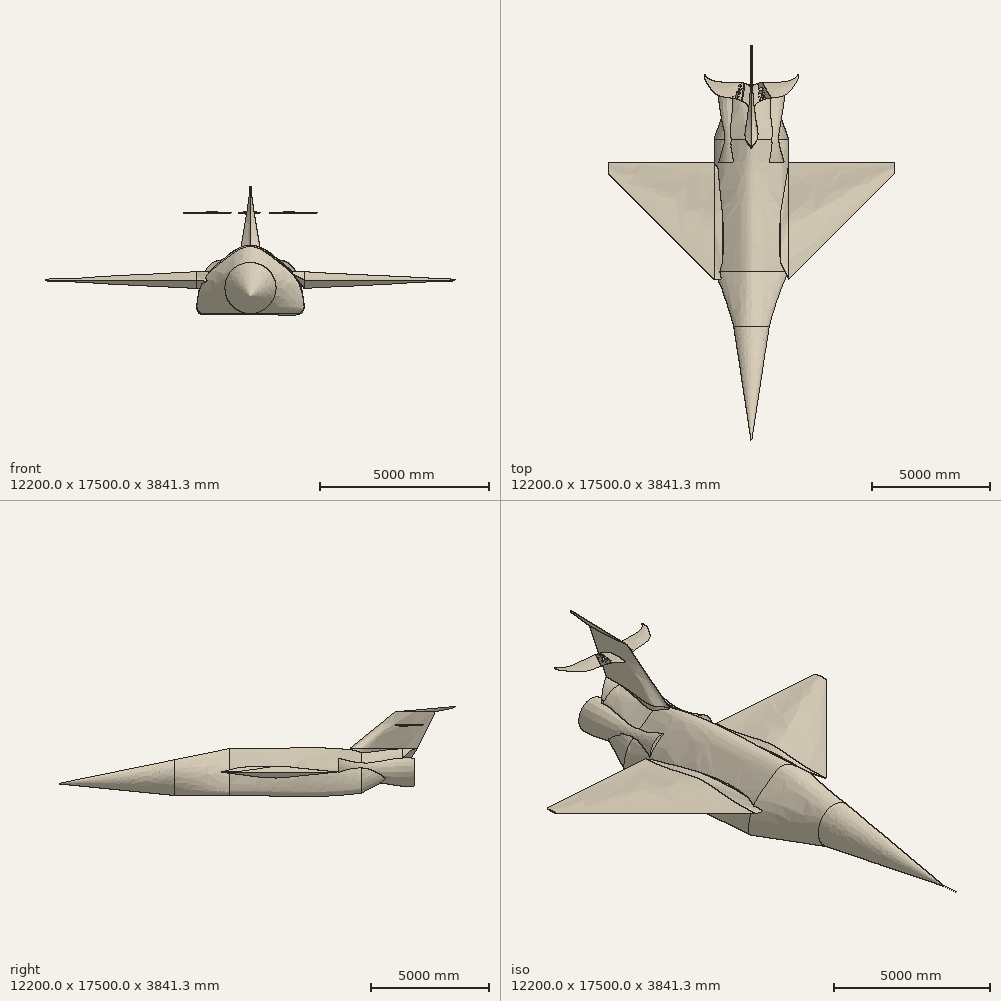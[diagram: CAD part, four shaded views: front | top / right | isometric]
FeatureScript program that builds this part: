
annotation { "Feature Type Name" : "Feature", "Feature Type Description" : "" }
export const myFeature = defineFeature(function(context is Context, id is Id, definition is map)
    precondition{}
    {
        {
            var Q0;
            Q0=qCreatedBy(makeId("Right.planeOp"),FACE);
            var sketch = newSketch(context, id + "F0", { "sketchPlane" : qUnion([Q0])});
            skLineSegment(sketch, "E0", {"start": v(0, 0) * mm, "end": v(-1750, 0) * mm});
            skLineSegment(sketch, "E1", {"start": v(-1750, 0) * mm, "end": v(-3500, 0) * mm});
            skLineSegment(sketch, "E2", {"start": v(-3500, 0) * mm, "end": v(-3500, -1000) * mm});
            skLineSegment(sketch, "E3", {"start": v(-3500, -1000) * mm, "end": v(-8500, -1000) * mm});
            skLineSegment(sketch, "E4", {"start": v(-8500, -1000) * mm, "end": v(-8500, -499.31) * mm});
            skLineSegment(sketch, "E5", {"start": v(-1151.4, 0) * mm, "end": v(-1151.4, 1000) * mm});
            skLineSegment(sketch, "E6", {"start": v(-1151.4, 1000) * mm, "end": v(-8500, -499.31) * mm});
            skLineSegment(sketch, "E7", {"start": v(-8500, -499.31) * mm, "end": v(-3500, -1000) * mm});
            skLineSegment(sketch, "E8", {"start": v(-3500, 0) * mm, "end": v(-3500, 520.82) * mm});
            skLineSegment(sketch, "E9", {"start": v(-8500, -499.31) * mm, "end": v(-8450, -499.31) * mm});
            skLineSegment(sketch, "E10", {"start": v(-8450, -499.31) * mm, "end": v(-8450, -489.1) * mm});
            skLineSegment(sketch, "E11", {"start": v(-8450, -499.31) * mm, "end": v(-8450, -504.32) * mm});
            skSolve(sketch);
        }
        {
            var Q0;
            Q0=sQuery(id+"F0.wireOp",EDGE,"E5");
            cPlane(context, id + "F1", {"entities" : qUnion([Q0]), "cplaneType" : CPlaneType.LINE_ANGLE, "offset" : 25 * mm, "angle" : 90 * degree, "oppositeDirection" : true, "width" : 150 * mm, "height" : 150 * mm});
        }
        {
            var Q0;
            Q0=qCreatedBy(id+"F1.planeOp",FACE);
            var sketch = newSketch(context, id + "F2", { "sketchPlane" : qUnion([Q0])});
            skLineSegment(sketch, "E12.top", {"start": v(-1394.2, -1000) * mm, "end": v(1394.2, -1000) * mm});
            skPoint(sketch, "E12.middle", {"position": v(0, 0) * mm});
            skFitSpline(sketch, "E13", {"points": [v(-1600, -1000) * mm, v(-848, 530) * mm, v(0, 1000) * mm, v(848, 530) * mm, v(1600, -1000) * mm], "startDerivative": vector(0, 10524.75) * mm, "endDerivative": vector(0, -10524.75) * mm});
            skArc(sketch, "E14", {"start": v(-735.27, 618.52) * mm, "mid": v(-1273.27, 435.52) * mm, "end": v(-1440.68, -107.53) * mm});
            skArc(sketch, "E15", {"start": v(1440.68, -107.53) * mm, "mid": v(1273.27, 435.52) * mm, "end": v(735.27, 618.52) * mm});
            skFitSpline(sketch, "E16.trimOffspring", {"points": [v(-1600, -1000) * mm, v(-848, 530) * mm, v(0, 1000) * mm, v(848, 530) * mm, v(1600, -1000) * mm], "startDerivative": vector(0, 10524.75) * mm, "endDerivative": vector(0, -10524.75) * mm});
            skFitSpline(sketch, "E17.trimOffspring", {"points": [v(-1600, -1000) * mm, v(-848, 530) * mm, v(0, 1000) * mm, v(848, 530) * mm, v(1600, -1000) * mm], "startDerivative": vector(0, 10524.75) * mm, "endDerivative": vector(0, -10524.75) * mm});
            skArc(sketch, "E18.filletArc", {"start": v(-1593.82, -787.83) * mm, "mid": v(-1539.85, -937.05) * mm, "end": v(-1394.2, -1000) * mm});
            skArc(sketch, "E19.filletArc", {"start": v(1394.2, -1000) * mm, "mid": v(1539.85, -937.05) * mm, "end": v(1593.82, -787.83) * mm});
            skSolve(sketch);
        }
        {
            var Q0;
            Q0=qCreatedBy(makeId("Front.planeOp"),FACE);
            var sketch = newSketch(context, id + "F3", { "sketchPlane" : qUnion([Q0])});
            skLineSegment(sketch, "E20.top", {"start": v(-1394.2, -1000) * mm, "end": v(1394.2, -1000) * mm});
            skPoint(sketch, "E20.middle", {"position": v(0, 0) * mm});
            skFitSpline(sketch, "E21", {"points": [v(-1600, -1000) * mm, v(-848, 530) * mm, v(0, 1000) * mm, v(848, 530) * mm, v(1600, -1000) * mm], "startDerivative": vector(0, 10524.75) * mm, "endDerivative": vector(0, -10524.75) * mm});
            skArc(sketch, "E22", {"start": v(-735.27, 618.52) * mm, "mid": v(-1273.27, 435.52) * mm, "end": v(-1440.68, -107.53) * mm});
            skArc(sketch, "E23", {"start": v(1440.68, -107.53) * mm, "mid": v(1273.27, 435.52) * mm, "end": v(735.27, 618.52) * mm});
            skFitSpline(sketch, "E24.trimOffspring", {"points": [v(-1600, -1000) * mm, v(-848, 530) * mm, v(0, 1000) * mm, v(848, 530) * mm, v(1600, -1000) * mm], "startDerivative": vector(0, 10524.75) * mm, "endDerivative": vector(0, -10524.75) * mm});
            skFitSpline(sketch, "E25.trimOffspring", {"points": [v(-1600, -1000) * mm, v(-848, 530) * mm, v(0, 1000) * mm, v(848, 530) * mm, v(1600, -1000) * mm], "startDerivative": vector(0, 10524.75) * mm, "endDerivative": vector(0, -10524.75) * mm});
            skArc(sketch, "E26.filletArc", {"start": v(-1593.82, -787.83) * mm, "mid": v(-1539.85, -937.05) * mm, "end": v(-1394.2, -1000) * mm});
            skArc(sketch, "E27.filletArc", {"start": v(1394.2, -1000) * mm, "mid": v(1539.85, -937.05) * mm, "end": v(1593.82, -787.83) * mm});
            skSolve(sketch);
        }
        {
            var Q0;
            Q0=qCreatedBy(makeId("Front.planeOp"),FACE);
            cPlane(context, id + "F4", {"entities" : qUnion([Q0]), "cplaneType" : CPlaneType.OFFSET, "offset" : 3500 * mm, "oppositeDirection" : true, "width" : 150 * mm, "height" : 150 * mm});
        }
        {
            var Q0;
            Q0=qCreatedBy(id+"F4.planeOp",FACE);
            var sketch = newSketch(context, id + "F5", { "sketchPlane" : qUnion([Q0])});
            skLineSegment(sketch, "E28.top", {"start": v(-1394.2, -1000) * mm, "end": v(1394.2, -1000) * mm});
            skPoint(sketch, "E28.middle", {"position": v(0, 0) * mm});
            skFitSpline(sketch, "E29", {"points": [v(-1600, -1000) * mm, v(-848, 530) * mm, v(0, 1000) * mm, v(848, 530) * mm, v(1600, -1000) * mm], "startDerivative": vector(0, 10524.75) * mm, "endDerivative": vector(0, -10524.75) * mm});
            skArc(sketch, "E30", {"start": v(-735.27, 618.52) * mm, "mid": v(-1273.27, 435.52) * mm, "end": v(-1440.68, -107.53) * mm});
            skArc(sketch, "E31", {"start": v(1440.68, -107.53) * mm, "mid": v(1273.27, 435.52) * mm, "end": v(735.27, 618.52) * mm});
            skFitSpline(sketch, "E32.trimOffspring", {"points": [v(-1600, -1000) * mm, v(-848, 530) * mm, v(0, 1000) * mm, v(848, 530) * mm, v(1600, -1000) * mm], "startDerivative": vector(0, 10524.75) * mm, "endDerivative": vector(0, -10524.75) * mm});
            skFitSpline(sketch, "E33.trimOffspring", {"points": [v(-1600, -1000) * mm, v(-848, 530) * mm, v(0, 1000) * mm, v(848, 530) * mm, v(1600, -1000) * mm], "startDerivative": vector(0, 10524.75) * mm, "endDerivative": vector(0, -10524.75) * mm});
            skArc(sketch, "E34.filletArc", {"start": v(-1593.82, -787.83) * mm, "mid": v(-1539.85, -937.05) * mm, "end": v(-1394.2, -1000) * mm});
            skArc(sketch, "E35.filletArc", {"start": v(1394.2, -1000) * mm, "mid": v(1539.85, -937.05) * mm, "end": v(1593.82, -787.83) * mm});
            skSolve(sketch);
        }
        {
            var Q0;
            Q0=qCreatedBy(makeId("Front.planeOp"),FACE);
            cPlane(context, id + "F6", {"entities" : qUnion([Q0]), "cplaneType" : CPlaneType.OFFSET, "offset" : 4500 * mm, "oppositeDirection" : true, "width" : 150 * mm, "height" : 150 * mm});
        }
        {
            var Q0;
            Q0=qCreatedBy(id+"F6.planeOp",FACE);
            var sketch = newSketch(context, id + "F7", { "sketchPlane" : qUnion([Q0])});
            skLineSegment(sketch, "E36.top", {"start": v(-1413.07, -900) * mm, "end": v(1413.07, -900) * mm});
            skPoint(sketch, "E36.middle", {"position": v(0, 0) * mm});
            skFitSpline(sketch, "E37", {"points": [v(-1600, -900) * mm, v(-784.42, 441.24) * mm, v(0, 900) * mm, v(784.42, 441.24) * mm, v(1600, -900) * mm], "startDerivative": vector(0, 9508.62) * mm, "endDerivative": vector(0, -9508.62) * mm});
            skArc(sketch, "E38", {"start": v(-719.25, 488.69) * mm, "mid": v(-1131.76, 394.84) * mm, "end": v(-1324.66, 18.33) * mm});
            skArc(sketch, "E39", {"start": v(1324.66, 18.33) * mm, "mid": v(1131.76, 394.84) * mm, "end": v(719.25, 488.69) * mm});
            skFitSpline(sketch, "E40.trimOffspring", {"points": [v(-1600, -900) * mm, v(-784.42, 441.24) * mm, v(0, 900) * mm, v(784.42, 441.24) * mm, v(1600, -900) * mm], "startDerivative": vector(0, 9508.62) * mm, "endDerivative": vector(0, -9508.62) * mm});
            skFitSpline(sketch, "E41.trimOffspring", {"points": [v(-1600, -900) * mm, v(-784.42, 441.24) * mm, v(0, 900) * mm, v(784.42, 441.24) * mm, v(1600, -900) * mm], "startDerivative": vector(0, 9508.62) * mm, "endDerivative": vector(0, -9508.62) * mm});
            skArc(sketch, "E42.filletArc", {"start": v(-1592.48, -705.43) * mm, "mid": v(-1545.4, -842.02) * mm, "end": v(-1413.07, -900) * mm});
            skArc(sketch, "E43.filletArc", {"start": v(1413.07, -900) * mm, "mid": v(1545.4, -842.02) * mm, "end": v(1592.48, -705.43) * mm});
            skLineSegment(sketch, "E44", {"start": v(-719.25, 488.69) * mm, "end": v(-1324.66, 18.33) * mm, "construction": true});
            skLineSegment(sketch, "E45", {"start": v(719.25, 488.69) * mm, "end": v(1324.66, 18.33) * mm, "construction": true});
            skSolve(sketch);
        }
        {
            var Q0;
            Q0=qCreatedBy(makeId("Front.planeOp"),FACE);
            cPlane(context, id + "F8", {"entities" : qUnion([Q0]), "cplaneType" : CPlaneType.OFFSET, "offset" : 6232.05 * mm, "oppositeDirection" : true, "width" : 150 * mm, "height" : 150 * mm});
        }
        {
            var Q0;
            Q0=qCreatedBy(id+"F8.planeOp",FACE);
            var sketch = newSketch(context, id + "F9", { "sketchPlane" : qUnion([Q0])});
            skArc(sketch, "E46", {"start": v(998.61, 52.63) * mm, "mid": v(0, 1000) * mm, "end": v(-998.61, 52.63) * mm});
            skLineSegment(sketch, "E47", {"start": v(0, 0) * mm, "end": v(-948.68, 0) * mm});
            skLineSegment(sketch, "E48", {"start": v(0, 0) * mm, "end": v(948.68, 0) * mm});
            skLineSegment(sketch, "E49", {"start": v(0, 1000) * mm, "end": v(0, 675) * mm, "construction": true});
            skLineSegment(sketch, "E50", {"start": v(0, 675) * mm, "end": v(-737.82, 675) * mm, "construction": true});
            skLineSegment(sketch, "E51", {"start": v(0, 675) * mm, "end": v(737.82, 675) * mm, "construction": true});
            skPoint(sketch, "E52.visualSharp", {"position": v(-1000, 0) * mm});
            skArc(sketch, "E52.filletArc", {"start": v(-998.61, 52.63) * mm, "mid": v(-984.96, 15.59) * mm, "end": v(-948.68, 0) * mm});
            skPoint(sketch, "E53.visualSharp", {"position": v(1000, 0) * mm});
            skArc(sketch, "E53.filletArc", {"start": v(948.68, 0) * mm, "mid": v(984.96, 15.59) * mm, "end": v(998.61, 52.63) * mm});
            skSolve(sketch);
        }
        {
            var Q0;
            Q0=makeQuery(id+"F2.imprint","IMPRINT",FACE,{"disambiguationData":[TD([[makeQuery(id+"F2.imprint","IMPRINT",EDGE,{"derivedFrom":sQuery(id+"F2.wireOp",EDGE,"E12.top")}),1.0]])]});
            var Q1;
            Q1=makeQuery(id+"F3.imprint","IMPRINT",FACE,{"disambiguationData":[TD([[makeQuery(id+"F3.imprint","IMPRINT",EDGE,{"derivedFrom":sQuery(id+"F3.wireOp",EDGE,"E20.top")}),1.0]])]});
            var Q2;
            Q2=makeQuery(id+"F5.imprint","IMPRINT",FACE,{"disambiguationData":[TD([[makeQuery(id+"F5.imprint","IMPRINT",EDGE,{"derivedFrom":sQuery(id+"F5.wireOp",EDGE,"E28.top")}),1.0]])]});
            var Q3;
            Q3=makeQuery(id+"F7.imprint","IMPRINT",FACE,{"disambiguationData":[TD([[makeQuery(id+"F7.imprint","IMPRINT",EDGE,{"derivedFrom":sQuery(id+"F7.wireOp",EDGE,"E36.top")}),1.0]])]});
            loft(context, id + "F10", {"sheetProfilesArray" : [{ "sheetProfileEntities" : qUnion([Q0]) }, { "sheetProfileEntities" : qUnion([Q1]) }, { "sheetProfileEntities" : qUnion([Q2]) }, { "sheetProfileEntities" : qUnion([Q3]) }]});
        }
        {
            var Q0;
            Q0=sQuery(id+"F7.wireOp",EDGE,"E44");
            var Q1;
            Q1=sQuery(id+"F9.wireOp",VERTEX,"E50.end");
            cPlane(context, id + "F11", {"entities" : qUnion([Q0, Q1]), "cplaneType" : CPlaneType.LINE_ANGLE, "offset" : 25 * mm, "angle" : 180 * degree, "width" : 150 * mm, "height" : 150 * mm});
        }
        {
            var Q0;
            Q0=qCreatedBy(id+"F11.planeOp",FACE);
            var sketch = newSketch(context, id + "F12", { "sketchPlane" : qUnion([Q0])});
            skLineSegment(sketch, "E54", {"start": v(-589.34, 4526.34) * mm, "end": v(-612.8, 6268.32) * mm});
            skLineSegment(sketch, "E55", {"start": v(-1354.08, 4472.19) * mm, "end": v(-612.8, 6268.32) * mm});
            skSolve(sketch);
        }
        {
            var Q0;
            Q0=sQuery(id+"F7.wireOp",EDGE,"E45");
            var Q1;
            Q1=sQuery(id+"F9.wireOp",VERTEX,"E51.end");
            cPlane(context, id + "F13", {"entities" : qUnion([Q0, Q1]), "cplaneType" : CPlaneType.LINE_ANGLE, "offset" : 25 * mm, "angle" : 0 * degree, "width" : 150 * mm, "height" : 150 * mm});
        }
        {
            var Q0;
            Q0=qCreatedBy(id+"F13.planeOp",FACE);
            var sketch = newSketch(context, id + "F14", { "sketchPlane" : qUnion([Q0])});
            skLineSegment(sketch, "E56", {"start": v(589.34, 4526.34) * mm, "end": v(612.8, 6268.32) * mm});
            skLineSegment(sketch, "E57", {"start": v(1354.08, 4472.19) * mm, "end": v(612.8, 6268.32) * mm});
            skSolve(sketch);
        }
        {
            var Q1;
            Q1=makeQuery(id+"F10.opLoft","CAP_FACE",FACE,{"disambiguationData":[OSD([makeQuery(id+"F7.imprint","IMPRINT",FACE,{"disambiguationData":[TD([[makeQuery(id+"F7.imprint","IMPRINT",EDGE,{"derivedFrom":sQuery(id+"F7.wireOp",EDGE,"E36.top")}),1.0]])]})])],"isStart":true});
            var Q2;
            Q2=makeQuery(id+"F9.imprint","IMPRINT",FACE,{"disambiguationData":[TD([[makeQuery(id+"F9.imprint","IMPRINT",EDGE,{"derivedFrom":sQuery(id+"F9.wireOp",EDGE,"E46")}),1.0]])]});
            var Q3;
            Q3=sQuery(id+"F12.wireOp",EDGE,"E54");
            var Q4;
            Q4=sQuery(id+"F14.wireOp",EDGE,"E56");
            loft(context, id + "F15", {"operationType" : NewBodyOperationType.ADD, "addGuides" : true, "sheetProfilesArray" : [{ "sheetProfileEntities" : qUnion([Q1]) }, { "sheetProfileEntities" : qUnion([Q2]) }], "guidesArray" : [{ "guideEntities" : qUnion([Q3]), "guideDerivativeType" : LoftGuideDerivativeType.DEFAULT, "guideDerivativeMagnitude" : 1 }, { "guideEntities" : qUnion([Q4]), "guideDerivativeType" : LoftGuideDerivativeType.DEFAULT, "guideDerivativeMagnitude" : 1 }]});
        }
        {
            var Q0;
            Q0=makeQuery(id+"F15.opLoft","CAP_FACE",FACE,{"disambiguationData":[OSD([makeQuery(id+"F9.imprint","IMPRINT",FACE,{"disambiguationData":[TD([[makeQuery(id+"F9.imprint","IMPRINT",EDGE,{"derivedFrom":sQuery(id+"F9.wireOp",EDGE,"E46")}),1.0]])]})])],"isStart":true});
            extrude(context, id + "F16", {"entities" : qUnion([Q0]), "operationType" : NewBodyOperationType.ADD, "depth" : 649.4 * mm, "offsetDistance" : 25 * mm});
        }
        {
            var Q0;
            Q0=qCreatedBy(makeId("Right.planeOp"),FACE);
            var sketch = newSketch(context, id + "F17", { "sketchPlane" : qUnion([Q0])});
            skLineSegment(sketch, "E58", {"start": v(0, 0) * mm, "end": v(4500, 0) * mm});
            skLineSegment(sketch, "E59", {"start": v(4500, 0) * mm, "end": v(6232.05, 0) * mm});
            skLineSegment(sketch, "E60", {"start": v(4500, 0) * mm, "end": v(4500, 1000) * mm});
            skLineSegment(sketch, "E61", {"start": v(4500, 1000) * mm, "end": v(6881.46, 1000) * mm});
            skLineSegment(sketch, "E62", {"start": v(6881.46, 1000) * mm, "end": v(6881.46, -1000) * mm});
            skLineSegment(sketch, "E63", {"start": v(6881.46, 1000) * mm, "end": v(6232.05, 0) * mm});
            skLineSegment(sketch, "E64", {"start": v(6232.05, 0) * mm, "end": v(5582.64, -1000) * mm});
            skLineSegment(sketch, "E65", {"start": v(5582.64, -1000) * mm, "end": v(6881.46, -1000) * mm});
            skSolve(sketch);
        }
        {
            var Q0;
            Q0=makeQuery(id+"F17.imprint","IMPRINT",FACE,{"disambiguationData":[TD([[makeQuery(id+"F17.imprint","IMPRINT",EDGE,{"derivedFrom":sQuery(id+"F17.wireOp",EDGE,"E62")}),-1.0]])]});
            var Q1;
            Q1=sQuery(id+"F17.wireOp",EDGE,"E61");
            revolve(context, id + "F18", {"operationType" : NewBodyOperationType.REMOVE, "entities" : qUnion([Q0]), "axis" : qUnion([Q1]), "revolveType" : RevolveType.SYMMETRIC, "oppositeDirection" : true, "angle" : 182 * degree});
        }
        {
            var Q0;
            Q0=qCreatedBy(id+"F1.planeOp",FACE);
            var sketch = newSketch(context, id + "F19", { "sketchPlane" : qUnion([Q0])});
            skLineSegment(sketch, "E66.top", {"start": v(-1394.2, -1000) * mm, "end": v(1394.2, -1000) * mm});
            skPoint(sketch, "E66.middle", {"position": v(0, 0) * mm});
            skFitSpline(sketch, "E67", {"points": [v(-1600, -1000) * mm, v(-848, 530) * mm, v(0, 1000) * mm, v(848, 530) * mm, v(1600, -1000) * mm], "startDerivative": vector(0, 10524.75) * mm, "endDerivative": vector(0, -10524.75) * mm});
            skArc(sketch, "E68.filletArc", {"start": v(-1593.82, -787.83) * mm, "mid": v(-1539.85, -937.05) * mm, "end": v(-1394.2, -1000) * mm});
            skArc(sketch, "E69.filletArc", {"start": v(1394.2, -1000) * mm, "mid": v(1539.85, -937.05) * mm, "end": v(1593.82, -787.83) * mm});
            skLineSegment(sketch, "E70", {"start": v(-1593.82, -787.83) * mm, "end": v(-1394.2, -1000) * mm, "construction": true});
            skLineSegment(sketch, "E71", {"start": v(1593.82, -787.83) * mm, "end": v(1394.2, -1000) * mm, "construction": true});
            skSolve(sketch);
        }
        {
            var Q0;
            Q0=qCreatedBy(makeId("Front.planeOp"),FACE);
            cPlane(context, id + "F20", {"entities" : qUnion([Q0]), "cplaneType" : CPlaneType.OFFSET, "offset" : 3500 * mm, "width" : 150 * mm, "height" : 150 * mm});
        }
        {
            var Q0;
            Q0=qCreatedBy(id+"F20.planeOp",FACE);
            var sketch = newSketch(context, id + "F21", { "sketchPlane" : qUnion([Q0])});
            skCircle(sketch, "E72", {"center": v(0, -239.59) * mm, "radius": 760.41 * mm});
            skLineSegment(sketch, "E73", {"start": v(0, -1000) * mm, "end": v(0, -800) * mm, "construction": true});
            skLineSegment(sketch, "E74", {"start": v(0, -800) * mm, "end": v(-513.97, -800) * mm, "construction": true});
            skLineSegment(sketch, "E75", {"start": v(0, -800) * mm, "end": v(513.97, -800) * mm, "construction": true});
            skSolve(sketch);
        }
        {
            var Q0;
            Q0=qCreatedBy(makeId("Front.planeOp"),FACE);
            cPlane(context, id + "F22", {"entities" : qUnion([Q0]), "cplaneType" : CPlaneType.OFFSET, "offset" : 8450 * mm, "width" : 150 * mm, "height" : 150 * mm});
        }
        {
            var Q0;
            Q0=qCreatedBy(id+"F22.planeOp",FACE);
            var sketch = newSketch(context, id + "F23", { "sketchPlane" : qUnion([Q0])});
            skCircle(sketch, "E76", {"center": v(0, -496.71) * mm, "radius": 7.6 * mm});
            skSolve(sketch);
        }
        {
            var Q0;
            Q0=sQuery(id+"F19.wireOp",EDGE,"E70");
            var Q1;
            Q1=sQuery(id+"F21.wireOp",VERTEX,"E74.end");
            cPlane(context, id + "F24", {"entities" : qUnion([Q0, Q1]), "cplaneType" : CPlaneType.LINE_ANGLE, "offset" : 25 * mm, "angle" : 0 * degree, "width" : 150 * mm, "height" : 150 * mm});
        }
        {
            var Q0;
            Q0=qCreatedBy(id+"F24.planeOp",FACE);
            var sketch = newSketch(context, id + "F25", { "sketchPlane" : qUnion([Q0])});
            skLineSegment(sketch, "E77", {"start": v(3032.27, -230.44) * mm, "end": v(558.11, 518.4) * mm});
            skLineSegment(sketch, "E78", {"start": v(3032.27, -230.44) * mm, "end": v(558.11, 227.09) * mm});
            skSolve(sketch);
        }
        {
            var Q0;
            Q0=sQuery(id+"F19.wireOp",EDGE,"E71");
            var Q1;
            Q1=sQuery(id+"F21.wireOp",VERTEX,"E75.end");
            cPlane(context, id + "F26", {"entities" : qUnion([Q0, Q1]), "cplaneType" : CPlaneType.LINE_ANGLE, "offset" : 25 * mm, "angle" : 180 * degree, "width" : 150 * mm, "height" : 150 * mm});
        }
        {
            var Q0;
            Q0=qCreatedBy(id+"F26.planeOp",FACE);
            var sketch = newSketch(context, id + "F27", { "sketchPlane" : qUnion([Q0])});
            skLineSegment(sketch, "E79", {"start": v(-3032.27, -230.44) * mm, "end": v(-558.11, 518.4) * mm});
            skLineSegment(sketch, "E80", {"start": v(-3032.27, -230.44) * mm, "end": v(-558.11, 227.09) * mm});
            skSolve(sketch);
        }
        {
            var Q1;
            Q1=makeQuery(id+"F19.imprint","IMPRINT",FACE,{"disambiguationData":[TD([[makeQuery(id+"F19.imprint","IMPRINT",EDGE,{"derivedFrom":sQuery(id+"F19.wireOp",EDGE,"E66.top")}),1.0]])]});
            var Q2;
            Q2=makeQuery(id+"F21.imprint","IMPRINT",FACE,{"disambiguationData":[TD([[makeQuery(id+"F21.imprint","IMPRINT",EDGE,{"derivedFrom":sQuery(id+"F21.wireOp",EDGE,"E72")}),1.0]])]});
            var Q3;
            Q3=sQuery(id+"F25.wireOp",EDGE,"E77");
            var Q4;
            Q4=sQuery(id+"F27.wireOp",EDGE,"E79");
            loft(context, id + "F28", {"operationType" : NewBodyOperationType.ADD, "addGuides" : true, "sheetProfilesArray" : [{ "sheetProfileEntities" : qUnion([Q1]) }, { "sheetProfileEntities" : qUnion([Q2]) }], "guidesArray" : [{ "guideEntities" : qUnion([Q3]), "guideDerivativeType" : LoftGuideDerivativeType.DEFAULT, "guideDerivativeMagnitude" : 1 }, { "guideEntities" : qUnion([Q4]), "guideDerivativeType" : LoftGuideDerivativeType.DEFAULT, "guideDerivativeMagnitude" : 1 }]});
        }
        {
            var Q1;
            Q1=makeQuery(id+"F28.opLoft","CAP_FACE",FACE,{"disambiguationData":[OSD([makeQuery(id+"F21.imprint","IMPRINT",FACE,{"disambiguationData":[TD([[makeQuery(id+"F21.imprint","IMPRINT",EDGE,{"derivedFrom":sQuery(id+"F21.wireOp",EDGE,"E72")}),1.0]])]})])],"isStart":true});
            var Q2;
            Q2=makeQuery(id+"F23.imprint","IMPRINT",FACE,{"disambiguationData":[TD([[makeQuery(id+"F23.imprint","IMPRINT",EDGE,{"derivedFrom":sQuery(id+"F23.wireOp",EDGE,"E76")}),1.0]])]});
            loft(context, id + "F29", {"operationType" : NewBodyOperationType.ADD, "sheetProfilesArray" : [{ "sheetProfileEntities" : qUnion([Q1]) }, { "sheetProfileEntities" : qUnion([Q2]) }]});
        }
        {
            var Q0;
            Q0=makeQuery(id+"F29.opLoft","CAP_FACE",FACE,{"disambiguationData":[OSD([makeQuery(id+"F23.imprint","IMPRINT",FACE,{"disambiguationData":[TD([[makeQuery(id+"F23.imprint","IMPRINT",EDGE,{"derivedFrom":sQuery(id+"F23.wireOp",EDGE,"E76")}),1.0]])]})])],"isStart":true});
            extrude(context, id + "F30", {"entities" : qUnion([Q0]), "operationType" : NewBodyOperationType.ADD, "depth" : 550 * mm, "offsetDistance" : 25 * mm});
        }
        {
            var Q0;
            Q0=qCreatedBy(makeId("Front.planeOp"),FACE);
            cPlane(context, id + "F31", {"entities" : qUnion([Q0]), "cplaneType" : CPlaneType.OFFSET, "offset" : 3500 * mm, "oppositeDirection" : true, "width" : 150 * mm, "height" : 150 * mm});
        }
        {
            var Q0;
            Q0=qCreatedBy(id+"F31.planeOp",FACE);
            var sketch = newSketch(context, id + "F32", { "sketchPlane" : qUnion([Q0])});
            skCircle(sketch, "E81", {"center": v(-800, 0) * mm, "radius": 600 * mm});
            skCircle(sketch, "E82", {"center": v(800, 0) * mm, "radius": 600 * mm});
            skSolve(sketch);
        }
        {
            var Q0;
            Q0=qCreatedBy(makeId("Front.planeOp"),FACE);
            cPlane(context, id + "F33", {"entities" : qUnion([Q0]), "cplaneType" : CPlaneType.OFFSET, "offset" : 4500 * mm, "oppositeDirection" : true, "width" : 150 * mm, "height" : 150 * mm});
        }
        {
            var Q0;
            Q0=qCreatedBy(id+"F33.planeOp",FACE);
            var sketch = newSketch(context, id + "F34", { "sketchPlane" : qUnion([Q0])});
            skCircle(sketch, "E83", {"center": v(-800, 0) * mm, "radius": 400 * mm});
            skCircle(sketch, "E84", {"center": v(800, 0) * mm, "radius": 400 * mm});
            skSolve(sketch);
        }
        {
            var Q0;
            Q0=qCreatedBy(makeId("Front.planeOp"),FACE);
            cPlane(context, id + "F35", {"entities" : qUnion([Q0]), "cplaneType" : CPlaneType.OFFSET, "offset" : 6232.05 * mm, "oppositeDirection" : true, "width" : 150 * mm, "height" : 150 * mm});
        }
        {
            var Q0;
            Q0=qCreatedBy(id+"F35.planeOp",FACE);
            var sketch = newSketch(context, id + "F36", { "sketchPlane" : qUnion([Q0])});
            skCircle(sketch, "E85", {"center": v(-800, 0) * mm, "radius": 600 * mm});
            skCircle(sketch, "E86", {"center": v(800, 0) * mm, "radius": 600 * mm});
            skSolve(sketch);
        }
        {
            var Q0;
            Q0=qCreatedBy(makeId("Front.planeOp"),FACE);
            cPlane(context, id + "F37", {"entities" : qUnion([Q0]), "cplaneType" : CPlaneType.OFFSET, "offset" : 6732.05 * mm, "oppositeDirection" : true, "width" : 150 * mm, "height" : 150 * mm});
        }
        {
            var Q0;
            Q0=qCreatedBy(id+"F37.planeOp",FACE);
            var sketch = newSketch(context, id + "F38", { "sketchPlane" : qUnion([Q0])});
            skCircle(sketch, "E87", {"center": v(-800, 0) * mm, "radius": 600 * mm});
            skCircle(sketch, "E88", {"center": v(800, 0) * mm, "radius": 600 * mm});
            skSolve(sketch);
        }
        {
            var Q0;
            Q0=makeQuery(id+"F32.imprint","IMPRINT",FACE,{"disambiguationData":[TD([[makeQuery(id+"F32.imprint","IMPRINT",EDGE,{"derivedFrom":sQuery(id+"F32.wireOp",EDGE,"E81")}),1.0]])]});
            var Q1;
            Q1=makeQuery(id+"F34.imprint","IMPRINT",FACE,{"disambiguationData":[TD([[makeQuery(id+"F34.imprint","IMPRINT",EDGE,{"derivedFrom":sQuery(id+"F34.wireOp",EDGE,"E83")}),1.0]])]});
            var Q2;
            Q2=makeQuery(id+"F36.imprint","IMPRINT",FACE,{"disambiguationData":[TD([[makeQuery(id+"F36.imprint","IMPRINT",EDGE,{"derivedFrom":sQuery(id+"F36.wireOp",EDGE,"E85")}),1.0]])]});
            var Q3;
            Q3=makeQuery(id+"F38.imprint","IMPRINT",FACE,{"disambiguationData":[TD([[makeQuery(id+"F38.imprint","IMPRINT",EDGE,{"derivedFrom":sQuery(id+"F38.wireOp",EDGE,"E87")}),1.0]])]});
            loft(context, id + "F39", {"sheetProfilesArray" : [{ "sheetProfileEntities" : qUnion([Q0]) }, { "sheetProfileEntities" : qUnion([Q1]) }, { "sheetProfileEntities" : qUnion([Q2]) }, { "sheetProfileEntities" : qUnion([Q3]) }]});
        }
        {
            var Q0;
            Q0=makeQuery(id+"F32.imprint","IMPRINT",FACE,{"disambiguationData":[TD([[makeQuery(id+"F32.imprint","IMPRINT",EDGE,{"derivedFrom":sQuery(id+"F32.wireOp",EDGE,"E82")}),1.0]])]});
            var Q1;
            Q1=makeQuery(id+"F34.imprint","IMPRINT",FACE,{"disambiguationData":[TD([[makeQuery(id+"F34.imprint","IMPRINT",EDGE,{"derivedFrom":sQuery(id+"F34.wireOp",EDGE,"E84")}),1.0]])]});
            var Q2;
            Q2=makeQuery(id+"F36.imprint","IMPRINT",FACE,{"disambiguationData":[TD([[makeQuery(id+"F36.imprint","IMPRINT",EDGE,{"derivedFrom":sQuery(id+"F36.wireOp",EDGE,"E86")}),1.0]])]});
            var Q3;
            Q3=makeQuery(id+"F38.imprint","IMPRINT",FACE,{"disambiguationData":[TD([[makeQuery(id+"F38.imprint","IMPRINT",EDGE,{"derivedFrom":sQuery(id+"F38.wireOp",EDGE,"E88")}),1.0]])]});
            loft(context, id + "F40", {"sheetProfilesArray" : [{ "sheetProfileEntities" : qUnion([Q0]) }, { "sheetProfileEntities" : qUnion([Q1]) }, { "sheetProfileEntities" : qUnion([Q2]) }, { "sheetProfileEntities" : qUnion([Q3]) }]});
        }
        {
            var Q0;
            Q0=qCreatedBy(makeId("Right.planeOp"),FACE);
            var sketch = newSketch(context, id + "F41", { "sketchPlane" : qUnion([Q0])});
            skFitSpline(sketch, "E89", {"points": [v(-1500, -50) * mm, v(0, 250) * mm, v(3000, -50) * mm, v(0, -250) * mm, v(-1500, -50) * mm]});
            skSolve(sketch);
        }
        {
            var Q0;
            Q0=qCreatedBy(makeId("Right.planeOp"),FACE);
            cPlane(context, id + "F42", {"entities" : qUnion([Q0]), "cplaneType" : CPlaneType.OFFSET, "offset" : 1600 * mm, "oppositeDirection" : true, "width" : 150 * mm, "height" : 150 * mm});
        }
        {
            var Q0;
            Q0=qCreatedBy(id+"F42.planeOp",FACE);
            var sketch = newSketch(context, id + "F43", { "sketchPlane" : qUnion([Q0])});
            skFitSpline(sketch, "E90", {"points": [v(-1500, 0) * mm, v(1000, 250) * mm, v(3500, 0) * mm], "startDerivative": vector(7500, 0) * mm, "endDerivative": vector(7500, 0) * mm});
            skFitSpline(sketch, "E91", {"points": [v(-1500, 0) * mm, v(1000, -250) * mm, v(3500, 0) * mm], "startDerivative": vector(5000, -750) * mm, "endDerivative": vector(7500, 0) * mm});
            skSolve(sketch);
        }
        {
            var Q0;
            Q0=qCreatedBy(makeId("Right.planeOp"),FACE);
            cPlane(context, id + "F44", {"entities" : qUnion([Q0]), "cplaneType" : CPlaneType.OFFSET, "offset" : 1600 * mm, "width" : 150 * mm, "height" : 150 * mm});
        }
        {
            var Q0;
            Q0=qCreatedBy(id+"F44.planeOp",FACE);
            var sketch = newSketch(context, id + "F45", { "sketchPlane" : qUnion([Q0])});
            skFitSpline(sketch, "E92", {"points": [v(-1500, 0) * mm, v(1000, 250) * mm, v(3500, 0) * mm], "startDerivative": vector(7500, 0) * mm, "endDerivative": vector(7500, 0) * mm});
            skFitSpline(sketch, "E93", {"points": [v(-1500, 0) * mm, v(1000, -250) * mm, v(3500, 0) * mm], "startDerivative": vector(5000, -750) * mm, "endDerivative": vector(7500, 0) * mm});
            skSolve(sketch);
        }
        {
            var Q0;
            Q0=qCreatedBy(makeId("Right.planeOp"),FACE);
            cPlane(context, id + "F46", {"entities" : qUnion([Q0]), "cplaneType" : CPlaneType.OFFSET, "offset" : 6100 * mm, "oppositeDirection" : true, "width" : 150 * mm, "height" : 150 * mm});
        }
        {
            var Q0;
            Q0=qCreatedBy(id+"F46.planeOp",FACE);
            var sketch = newSketch(context, id + "F47", { "sketchPlane" : qUnion([Q0])});
            skFitSpline(sketch, "E94", {"points": [v(3000, 0) * mm, v(3250, 25) * mm, v(3500, 0) * mm], "startDerivative": vector(750, 0) * mm, "endDerivative": vector(750, 0) * mm});
            skFitSpline(sketch, "E95", {"points": [v(3000, 0) * mm, v(3250, -25) * mm, v(3500, 0) * mm], "startDerivative": vector(500, -75) * mm, "endDerivative": vector(750, 0) * mm});
            skSolve(sketch);
        }
        {
            var Q0;
            Q0=qCreatedBy(makeId("Right.planeOp"),FACE);
            cPlane(context, id + "F48", {"entities" : qUnion([Q0]), "cplaneType" : CPlaneType.OFFSET, "offset" : 6100 * mm, "width" : 150 * mm, "height" : 150 * mm});
        }
        {
            var Q0;
            Q0=qCreatedBy(id+"F48.planeOp",FACE);
            var sketch = newSketch(context, id + "F49", { "sketchPlane" : qUnion([Q0])});
            skFitSpline(sketch, "E96", {"points": [v(3000, 0) * mm, v(3250, 25) * mm, v(3500, 0) * mm], "startDerivative": vector(750, 0) * mm, "endDerivative": vector(750, 0) * mm});
            skFitSpline(sketch, "E97", {"points": [v(3000, 0) * mm, v(3250, -25) * mm, v(3500, 0) * mm], "startDerivative": vector(500, -75) * mm, "endDerivative": vector(750, 0) * mm});
            skSolve(sketch);
        }
        {
            var Q0;
            Q0=qSketchRegion(id+"F41",true);
            extrude(context, id + "F50", {"entities" : qUnion([Q0]), "endBound" : BoundingType.SYMMETRIC, "depth" : 2500 * mm, "offsetDistance" : 25 * mm});
        }
        {
            var Q1;
            Q1=makeQuery(id+"F50.opExtrude","CAP_FACE",FACE,{"disambiguationData":[OSD([sQuery(id+"F41.wireOp",EDGE,"E89")])],"isStart":true});
            var Q2;
            {var subQ0=sQuery(id+"F43.wireOp",EDGE,"E90");Q2=makeQuery(id+"F43.imprint","IMPRINT",FACE,{"disambiguationData":[TD([[makeQuery(id+"F43.imprint","IMPRINT",EDGE,{"derivedFrom":subQ0}),-1.0]])]});}
            loft(context, id + "F51", {"operationType" : NewBodyOperationType.ADD, "sheetProfilesArray" : [{ "sheetProfileEntities" : qUnion([Q1]) }, { "sheetProfileEntities" : qUnion([Q2]) }]});
        }
        {
            var Q1;
            Q1=makeQuery(id+"F50.opExtrude","CAP_FACE",FACE,{"disambiguationData":[OSD([sQuery(id+"F41.wireOp",EDGE,"E89")])],"isStart":false});
            var Q2;
            {var subQ0=sQuery(id+"F45.wireOp",EDGE,"E92");Q2=makeQuery(id+"F45.imprint","IMPRINT",FACE,{"disambiguationData":[TD([[makeQuery(id+"F45.imprint","IMPRINT",EDGE,{"derivedFrom":subQ0}),-1.0]])]});}
            loft(context, id + "F52", {"operationType" : NewBodyOperationType.ADD, "sheetProfilesArray" : [{ "sheetProfileEntities" : qUnion([Q1]) }, { "sheetProfileEntities" : qUnion([Q2]) }]});
        }
        {
            var Q1;
            {var subQ0=sQuery(id+"F43.wireOp",EDGE,"E90");Q1=makeQuery(id+"F51.opLoft","CAP_FACE",FACE,{"disambiguationData":[OSD([makeQuery(id+"F43.imprint","IMPRINT",FACE,{"disambiguationData":[TD([[makeQuery(id+"F43.imprint","IMPRINT",EDGE,{"derivedFrom":subQ0}),-1.0]])]})])],"isStart":true});}
            var Q2;
            {var subQ0=sQuery(id+"F47.wireOp",EDGE,"E94");Q2=makeQuery(id+"F47.imprint","IMPRINT",FACE,{"disambiguationData":[TD([[makeQuery(id+"F47.imprint","IMPRINT",EDGE,{"derivedFrom":subQ0}),-1.0]])]});}
            loft(context, id + "F53", {"operationType" : NewBodyOperationType.ADD, "sheetProfilesArray" : [{ "sheetProfileEntities" : qUnion([Q1]) }, { "sheetProfileEntities" : qUnion([Q2]) }]});
        }
        {
            var Q1;
            {var subQ0=sQuery(id+"F45.wireOp",EDGE,"E92");Q1=makeQuery(id+"F52.opLoft","CAP_FACE",FACE,{"disambiguationData":[OSD([makeQuery(id+"F45.imprint","IMPRINT",FACE,{"disambiguationData":[TD([[makeQuery(id+"F45.imprint","IMPRINT",EDGE,{"derivedFrom":subQ0}),-1.0]])]})])],"isStart":true});}
            var Q2;
            {var subQ0=sQuery(id+"F49.wireOp",EDGE,"E96");Q2=makeQuery(id+"F49.imprint","IMPRINT",FACE,{"disambiguationData":[TD([[makeQuery(id+"F49.imprint","IMPRINT",EDGE,{"derivedFrom":subQ0}),-1.0]])]});}
            loft(context, id + "F54", {"operationType" : NewBodyOperationType.ADD, "sheetProfilesArray" : [{ "sheetProfileEntities" : qUnion([Q1]) }, { "sheetProfileEntities" : qUnion([Q2]) }]});
        }
        {
            var Q0;
            Q0=qCreatedBy(makeId("Right.planeOp"),FACE);
            var sketch = newSketch(context, id + "F55", { "sketchPlane" : qUnion([Q0])});
            skLineSegment(sketch, "E98", {"start": v(0, 0) * mm, "end": v(4500, 0) * mm});
            skLineSegment(sketch, "E99", {"start": v(4500, 0) * mm, "end": v(4500, 1000) * mm});
            skLineSegment(sketch, "E100", {"start": v(4500, 1000) * mm, "end": v(4500, 750) * mm});
            skLineSegment(sketch, "E101", {"start": v(4500, 750) * mm, "end": v(4000, 750) * mm});
            skLineSegment(sketch, "E102", {"start": v(4500, 750) * mm, "end": v(6250, 750) * mm});
            skLineSegment(sketch, "E103", {"start": v(4500, 1000) * mm, "end": v(4000, 1000) * mm});
            skLineSegment(sketch, "E104", {"start": v(4500, 1000) * mm, "end": v(6881.46, 1000) * mm});
            skLineSegment(sketch, "E105", {"start": v(6881.46, 1000) * mm, "end": v(8500, 1000) * mm});
            skLineSegment(sketch, "E106", {"start": v(8500, 1000) * mm, "end": v(8500, 2800) * mm});
            skLineSegment(sketch, "E107", {"start": v(6881.46, 1000) * mm, "end": v(7648.6, 2572.89) * mm});
            skLineSegment(sketch, "E108", {"start": v(7648.6, 2572.89) * mm, "end": v(5943.2, 2572.89) * mm});
            skLineSegment(sketch, "E109", {"start": v(5943.2, 2572.89) * mm, "end": v(4000, 1000) * mm});
            skSolve(sketch);
        }
        {
            var Q0;
            Q0=qCreatedBy(makeId("Top.planeOp"),FACE);
            cPlane(context, id + "F56", {"entities" : qUnion([Q0]), "cplaneType" : CPlaneType.OFFSET, "offset" : 750 * mm, "width" : 150 * mm, "height" : 150 * mm});
        }
        {
            var Q0;
            Q0=qCreatedBy(id+"F56.planeOp",FACE);
            var sketch = newSketch(context, id + "F57", { "sketchPlane" : qUnion([Q0])});
            skFitSpline(sketch, "E110", {"points": [v(0, 4000) * mm, v(-250, 4500) * mm, v(0, 6250) * mm], "startDerivative": vector(-889.86, 1147.1) * mm, "endDerivative": vector(737.87, 3164.53) * mm});
            skFitSpline(sketch, "E111", {"points": [v(0, 4000) * mm, v(250, 4500) * mm, v(0, 6250) * mm], "startDerivative": vector(889.86, 1147.1) * mm, "endDerivative": vector(-737.87, 3164.53) * mm});
            skSolve(sketch);
        }
        {
            var Q0;
            Q0=qCreatedBy(makeId("Top.planeOp"),FACE);
            cPlane(context, id + "F58", {"entities" : qUnion([Q0]), "cplaneType" : CPlaneType.OFFSET, "offset" : 1000 * mm, "width" : 150 * mm, "height" : 150 * mm});
        }
        {
            var Q0;
            Q0=qCreatedBy(id+"F58.planeOp",FACE);
            var sketch = newSketch(context, id + "F59", { "sketchPlane" : qUnion([Q0])});
            skFitSpline(sketch, "E112", {"points": [v(0, 4000) * mm, v(-250, 4500) * mm, v(0, 6881.46) * mm], "startDerivative": vector(0, 2302.24) * mm, "endDerivative": vector(0, 5298.17) * mm});
            skFitSpline(sketch, "E113", {"points": [v(0, 4000) * mm, v(250, 4500) * mm, v(0, 6881.46) * mm], "startDerivative": vector(0, 2302.24) * mm, "endDerivative": vector(0, 5298.17) * mm});
            skSolve(sketch);
        }
        {
            var Q0;
            Q0=sQuery(id+"F55.wireOp",EDGE,"E108");
            cPlane(context, id + "F60", {"entities" : qUnion([Q0]), "cplaneType" : CPlaneType.LINE_ANGLE, "offset" : 25 * mm, "angle" : 180 * degree, "width" : 150 * mm, "height" : 150 * mm});
        }
        {
            var Q0;
            Q0=qCreatedBy(id+"F60.planeOp",FACE);
            var sketch = newSketch(context, id + "F61", { "sketchPlane" : qUnion([Q0])});
            skFitSpline(sketch, "E114", {"points": [v(0, 5943.2) * mm, v(-25, 6795.9) * mm, v(0, 7648.6) * mm], "startDerivative": vector(-75, 1705.4) * mm, "endDerivative": vector(75, 1705.4) * mm});
            skFitSpline(sketch, "E115", {"points": [v(0, 5943.2) * mm, v(25, 6795.9) * mm, v(0, 7648.6) * mm], "startDerivative": vector(75, 1705.4) * mm, "endDerivative": vector(-75, 1705.4) * mm});
            skSolve(sketch);
        }
        {
            var Q0;
            Q0=qCreatedBy(makeId("Front.planeOp"),FACE);
            cPlane(context, id + "F62", {"entities" : qUnion([Q0]), "cplaneType" : CPlaneType.OFFSET, "offset" : 8500 * mm, "oppositeDirection" : true, "width" : 150 * mm, "height" : 150 * mm});
        }
        {
            var Q0;
            Q0=qCreatedBy(id+"F62.planeOp",FACE);
            var sketch = newSketch(context, id + "F63", { "sketchPlane" : qUnion([Q0])});
            skCircle(sketch, "E116", {"center": v(0, 2775) * mm, "radius": 25 * mm});
            skSolve(sketch);
        }
        {
            var Q0;
            Q0=qCreatedBy(makeId("Right.planeOp"),FACE);
            var sketch = newSketch(context, id + "F64", { "sketchPlane" : qUnion([Q0])});
            skLineSegment(sketch, "E117", {"start": v(5943.2, 2572.89) * mm, "end": v(8500, 2800) * mm});
            skSolve(sketch);
        }
        {
            var Q1;
            Q1 = qSketchRegion(id + "F57", true);
            var Q2;
            Q2 = qSketchRegion(id + "F59", true);
            loft(context, id + "F65", {"sheetProfilesArray" : [{ "sheetProfileEntities" : qUnion([Q1]) }, { "sheetProfileEntities" : qUnion([Q2]) }]});
        }
        {
            var Q1;
            {var subQ0=sQuery(id+"F59.wireOp",EDGE,"E112");Q1=makeQuery(id+"F65.opLoft","CAP_FACE",FACE,{"disambiguationData":[OSD([makeQuery(id+"F59.imprint","IMPRINT",FACE,{"disambiguationData":[TD([[makeQuery(id+"F59.imprint","IMPRINT",EDGE,{"derivedFrom":subQ0}),-1.0]])]})])],"isStart":true});}
            var Q2;
            Q2=makeQuery(id+"F61.imprint","IMPRINT",FACE,{"disambiguationData":[TD([[makeQuery(id+"F61.imprint","IMPRINT",EDGE,{"derivedFrom":sQuery(id+"F61.wireOp",EDGE,"E114")}),-1.0]])]});
            loft(context, id + "F66", {"operationType" : NewBodyOperationType.ADD, "sheetProfilesArray" : [{ "sheetProfileEntities" : qUnion([Q1]) }, { "sheetProfileEntities" : qUnion([Q2]) }]});
        }
        {
            var Q1;
            Q1=makeQuery(id+"F66.opLoft","CAP_FACE",FACE,{"disambiguationData":[OSD([makeQuery(id+"F61.imprint","IMPRINT",FACE,{"disambiguationData":[TD([[makeQuery(id+"F61.imprint","IMPRINT",EDGE,{"derivedFrom":sQuery(id+"F61.wireOp",EDGE,"E114")}),-1.0]])]})])],"isStart":true});
            var Q2;
            Q2=makeQuery(id+"F63.imprint","IMPRINT",FACE,{"disambiguationData":[TD([[makeQuery(id+"F63.imprint","IMPRINT",EDGE,{"derivedFrom":sQuery(id+"F63.wireOp",EDGE,"E116")}),1.0]])]});
            var Q3;
            Q3=sQuery(id+"F64.wireOp",EDGE,"E117");
            loft(context, id + "F67", {"operationType" : NewBodyOperationType.ADD, "addGuides" : true, "sheetProfilesArray" : [{ "sheetProfileEntities" : qUnion([Q1]) }, { "sheetProfileEntities" : qUnion([Q2]) }], "guidesArray" : [{ "guideEntities" : qUnion([Q3]), "guideDerivativeType" : LoftGuideDerivativeType.DEFAULT, "guideDerivativeMagnitude" : 1 }]});
        }
        {
            var Q0;
            Q0=qCreatedBy(makeId("Top.planeOp"),FACE);
            cPlane(context, id + "F68", {"entities" : qUnion([Q0]), "cplaneType" : CPlaneType.OFFSET, "offset" : 2000 * mm, "width" : 150 * mm, "height" : 150 * mm});
        }
        {
            var Q0;
            Q0=qCreatedBy(id+"F68.planeOp",FACE);
            var sketch = newSketch(context, id + "F69", { "sketchPlane" : qUnion([Q0])});
            skLineSegment(sketch, "E118", {"start": v(0, 0) * mm, "end": v(0, 4500) * mm});
            skLineSegment(sketch, "E119", {"start": v(0, 4500) * mm, "end": v(0, 7369.2) * mm});
            skLineSegment(sketch, "E120", {"start": v(0, 7369.2) * mm, "end": v(0, 5235.43) * mm});
            skLineSegment(sketch, "E121", {"start": v(0, 6302.31) * mm, "end": v(0, 5302.31) * mm});
            skLineSegment(sketch, "E122", {"start": v(0, 6302.31) * mm, "end": v(0, 7302.31) * mm});
            skLineSegment(sketch, "E123", {"start": v(0, 6302.31) * mm, "end": v(0, 6552.31) * mm});
            skLineSegment(sketch, "E124", {"start": v(0, 6302.31) * mm, "end": v(-1200, 6302.31) * mm});
            skLineSegment(sketch, "E125", {"start": v(0, 6302.31) * mm, "end": v(1200, 6302.31) * mm});
            skLineSegment(sketch, "E126", {"start": v(0, 6552.31) * mm, "end": v(-1700, 6552.31) * mm});
            skLineSegment(sketch, "E127", {"start": v(0, 6552.31) * mm, "end": v(1700, 6552.31) * mm});
            skLineSegment(sketch, "E128", {"start": v(0, 7302.31) * mm, "end": v(-2000, 7302.31) * mm});
            skLineSegment(sketch, "E129", {"start": v(0, 7302.31) * mm, "end": v(2000, 7302.31) * mm});
            skLineSegment(sketch, "E130", {"start": v(-2000, 7302.31) * mm, "end": v(-2000, 7052.31) * mm});
            skLineSegment(sketch, "E131", {"start": v(2000, 7302.31) * mm, "end": v(2000, 7052.31) * mm});
            skFitSpline(sketch, "E132", {"points": [v(0, 5302.31) * mm, v(-1200, 6302.31) * mm, v(-2000, 7052.31) * mm], "startDerivative": vector(0, 5513.6) * mm, "endDerivative": vector(-1974.16, 3290.27) * mm});
            skFitSpline(sketch, "E133", {"points": [v(0, 5302.31) * mm, v(1200, 6302.31) * mm, v(2000, 7052.31) * mm], "startDerivative": vector(0, 5513.6) * mm, "endDerivative": vector(1974.16, 3290.27) * mm});
            skFitSpline(sketch, "E134", {"points": [v(0, 6552.31) * mm, v(-2000, 7302.31) * mm], "startDerivative": vector(0, 2250) * mm, "endDerivative": vector(-900, 2250) * mm});
            skFitSpline(sketch, "E135", {"points": [v(0, 6552.31) * mm, v(2000, 7302.31) * mm], "startDerivative": vector(0, 2250) * mm, "endDerivative": vector(900, 2250) * mm});
            skSolve(sketch);
        }
        {
            var Q0;
            Q0=qCreatedBy(makeId("Right.planeOp"),FACE);
            var sketch = newSketch(context, id + "F70", { "sketchPlane" : qUnion([Q0])});
            skFitSpline(sketch, "E136", {"points": [v(5302.31, 2000) * mm, v(5927.31, 2050) * mm, v(6552.31, 2000) * mm], "startDerivative": vector(1250, 150) * mm, "endDerivative": vector(1250, -150) * mm});
            skFitSpline(sketch, "E137", {"points": [v(5302.31, 2000) * mm, v(5927.31, 1950) * mm, v(6552.31, 2000) * mm], "startDerivative": vector(1250, -150) * mm, "endDerivative": vector(1250, 150) * mm});
            skSolve(sketch);
        }
        {
            var Q0;
            Q0=qCreatedBy(makeId("Right.planeOp"),FACE);
            cPlane(context, id + "F71", {"entities" : qUnion([Q0]), "cplaneType" : CPlaneType.OFFSET, "offset" : 2000 * mm, "oppositeDirection" : true, "width" : 150 * mm, "height" : 150 * mm});
        }
        {
            var Q0;
            Q0=qCreatedBy(id+"F71.planeOp",FACE);
            var sketch = newSketch(context, id + "F72", { "sketchPlane" : qUnion([Q0])});
            skFitSpline(sketch, "E138", {"points": [v(7052.31, 2000) * mm, v(7177.31, 2010) * mm, v(7302.31, 2000) * mm], "startDerivative": vector(250, 30) * mm, "endDerivative": vector(250, -30) * mm});
            skFitSpline(sketch, "E139", {"points": [v(7052.31, 2000) * mm, v(7177.31, 1990) * mm, v(7302.31, 2000) * mm], "startDerivative": vector(250, -30) * mm, "endDerivative": vector(250, 30) * mm});
            skSolve(sketch);
        }
        {
            var Q0;
            Q0=qCreatedBy(makeId("Right.planeOp"),FACE);
            cPlane(context, id + "F73", {"entities" : qUnion([Q0]), "cplaneType" : CPlaneType.OFFSET, "offset" : 2000 * mm, "width" : 150 * mm, "height" : 150 * mm});
        }
        {
            var Q0;
            Q0=qCreatedBy(id+"F73.planeOp",FACE);
            var sketch = newSketch(context, id + "F74", { "sketchPlane" : qUnion([Q0])});
            skFitSpline(sketch, "E140", {"points": [v(7052.31, 2000) * mm, v(7177.31, 2010) * mm, v(7302.31, 2000) * mm], "startDerivative": vector(250, 30) * mm, "endDerivative": vector(250, -30) * mm});
            skFitSpline(sketch, "E141", {"points": [v(7052.31, 2000) * mm, v(7177.31, 1990) * mm, v(7302.31, 2000) * mm], "startDerivative": vector(250, -30) * mm, "endDerivative": vector(250, 30) * mm});
            skSolve(sketch);
        }
        {
            var Q1;
            Q1 = qSketchRegion(id + "F70", true);
            var Q2;
            Q2=makeQuery(id+"F72.imprint","IMPRINT",FACE,{"disambiguationData":[TD([[makeQuery(id+"F72.imprint","IMPRINT",EDGE,{"derivedFrom":sQuery(id+"F72.wireOp",EDGE,"E138")}),-1.0]])]});
            var Q3;
            Q3=sQuery(id+"F69.wireOp",EDGE,"E132");
            var Q4;
            Q4=sQuery(id+"F69.wireOp",EDGE,"E134");
            loft(context, id + "F75", {"addGuides" : true, "sheetProfilesArray" : [{ "sheetProfileEntities" : qUnion([Q1]) }, { "sheetProfileEntities" : qUnion([Q2]) }], "guidesArray" : [{ "guideEntities" : qUnion([Q3]), "guideDerivativeType" : LoftGuideDerivativeType.DEFAULT, "guideDerivativeMagnitude" : 1 }, { "guideEntities" : qUnion([Q4]), "guideDerivativeType" : LoftGuideDerivativeType.DEFAULT, "guideDerivativeMagnitude" : 1 }]});
        }
        {
            var Q1;
            Q1 = qSketchRegion(id + "F70", true);
            var Q2;
            Q2=makeQuery(id+"F74.imprint","IMPRINT",FACE,{"disambiguationData":[TD([[makeQuery(id+"F74.imprint","IMPRINT",EDGE,{"derivedFrom":sQuery(id+"F74.wireOp",EDGE,"E140")}),-1.0]])]});
            var Q3;
            Q3=sQuery(id+"F69.wireOp",EDGE,"E133");
            var Q4;
            Q4=sQuery(id+"F69.wireOp",EDGE,"E135");
            loft(context, id + "F76", {"operationType" : NewBodyOperationType.ADD, "addGuides" : true, "sheetProfilesArray" : [{ "sheetProfileEntities" : qUnion([Q1]) }, { "sheetProfileEntities" : qUnion([Q2]) }], "guidesArray" : [{ "guideEntities" : qUnion([Q3]), "guideDerivativeType" : LoftGuideDerivativeType.DEFAULT, "guideDerivativeMagnitude" : 1 }, { "guideEntities" : qUnion([Q4]), "guideDerivativeType" : LoftGuideDerivativeType.DEFAULT, "guideDerivativeMagnitude" : 1 }]});
        }
    });
